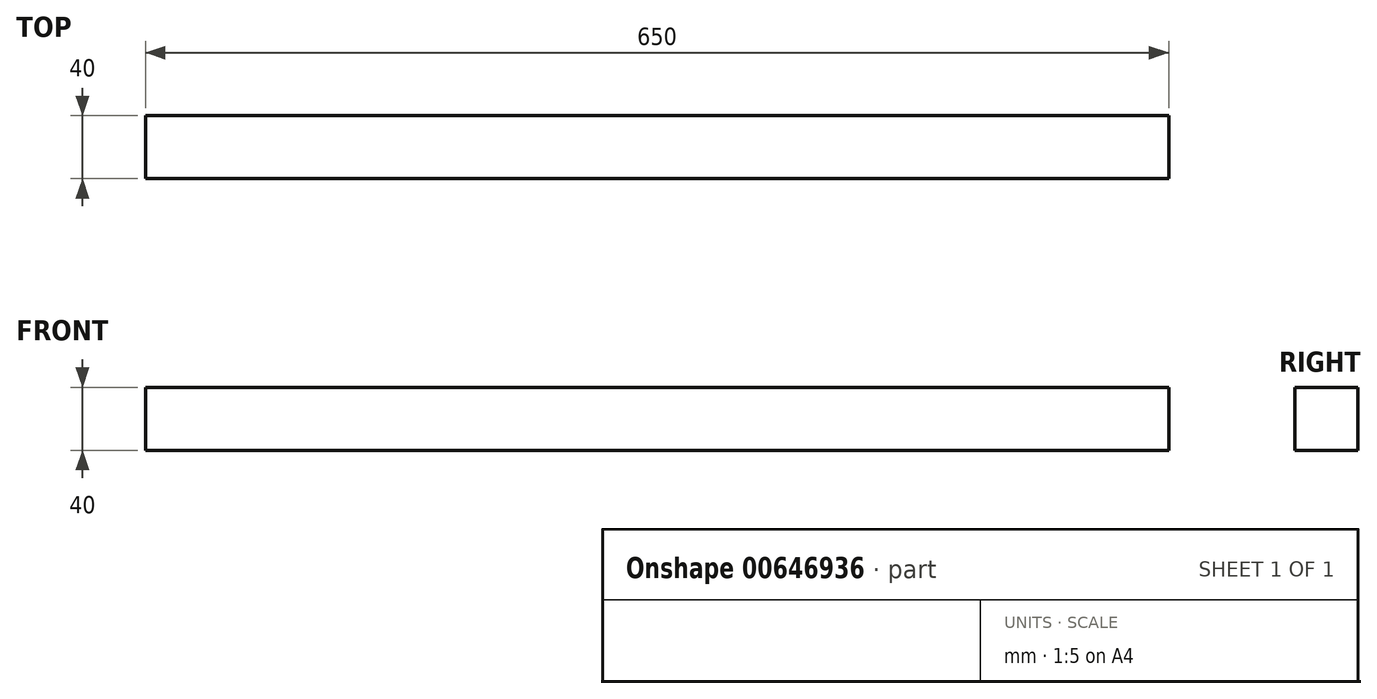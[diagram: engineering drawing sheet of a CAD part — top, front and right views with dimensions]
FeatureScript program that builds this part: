
annotation { "Feature Type Name" : "Feature", "Feature Type Description" : "" }
export const myFeature = defineFeature(function(context is Context, id is Id, definition is map)
    precondition{}
    {
        {
            var Q0;
            Q0=qCreatedBy(makeId("Top.planeOp"),FACE);
            var sketch = newSketch(context, id + "F0", { "sketchPlane" : qUnion([Q0])});
            skLineSegment(sketch, "E0.bottom", {"start": v(-325, 20) * mm, "end": v(325, 20) * mm});
            skLineSegment(sketch, "E0.top", {"start": v(-325, -20) * mm, "end": v(325, -20) * mm});
            skLineSegment(sketch, "E0.left", {"start": v(-325, 20) * mm, "end": v(-325, -20) * mm});
            skLineSegment(sketch, "E0.right", {"start": v(325, 20) * mm, "end": v(325, -20) * mm});
            skSolve(sketch);
        }
        {
            var Q0;
            Q0 = qSketchRegion(id + "F0", true);
            extrude(context, id + "F1", {"entities" : qUnion([Q0]), "endBound" : BoundingType.SYMMETRIC, "depth" : 40 * mm, "offsetDistance" : 25 * mm});
        }
    });
